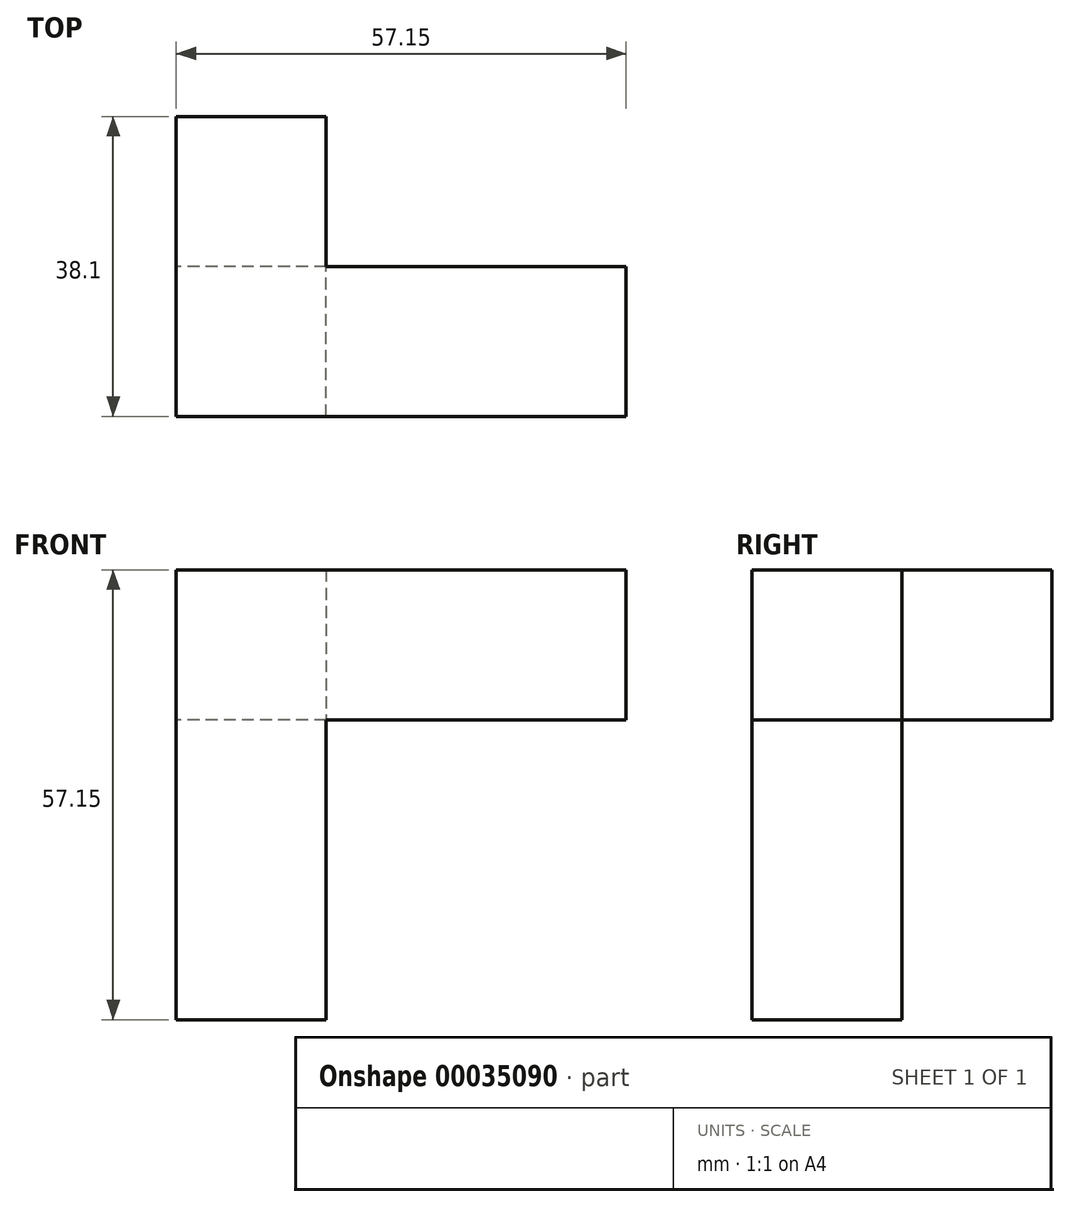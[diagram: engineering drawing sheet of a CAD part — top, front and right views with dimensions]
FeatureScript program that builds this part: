
annotation { "Feature Type Name" : "Feature", "Feature Type Description" : "" }
export const myFeature = defineFeature(function(context is Context, id is Id, definition is map)
    precondition{}
    {
        {
            var Q0;
            Q0=qCreatedBy(makeId("Front.planeOp"),FACE);
            var sketch = newSketch(context, id + "F0", { "sketchPlane" : qUnion([Q0])});
            skLineSegment(sketch, "E0", {"start": v(-68.52, -6.83) * mm, "end": v(-11.37, -6.83) * mm});
            skLineSegment(sketch, "E1", {"start": v(-11.37, -6.83) * mm, "end": v(-11.37, -25.88) * mm});
            skLineSegment(sketch, "E2", {"start": v(-68.52, -6.83) * mm, "end": v(-68.52, -25.88) * mm});
            skLineSegment(sketch, "E3", {"start": v(-68.52, -25.88) * mm, "end": v(-11.37, -25.88) * mm});
            skLineSegment(sketch, "E4", {"start": v(-68.52, -25.88) * mm, "end": v(-68.52, -63.98) * mm});
            skLineSegment(sketch, "E5", {"start": v(-68.52, -63.98) * mm, "end": v(-49.47, -63.98) * mm});
            skLineSegment(sketch, "E6", {"start": v(-49.47, -63.98) * mm, "end": v(-49.47, -25.88) * mm});
            skSolve(sketch);
        }
        {
            var Q0;
            Q0 = qSketchRegion(id + "F0", true);
            extrude(context, id + "F1", {"entities" : qUnion([Q0]), "depth" : 19.05 * mm});
        }
        {
            var Q0;
            Q0=makeQuery(id+"F1.opExtrude","CAP_FACE",FACE,{"disambiguationData":[OSD([sQuery(id+"F0.wireOp",EDGE,"E0"),sQuery(id+"F0.wireOp",EDGE,"E1"),sQuery(id+"F0.wireOp",EDGE,"E2"),sQuery(id+"F0.wireOp",EDGE,"E3"),sQuery(id+"F0.wireOp",EDGE,"E4"),sQuery(id+"F0.wireOp",EDGE,"E5"),sQuery(id+"F0.wireOp",EDGE,"E6")])],"isStart":true});
            var sketch = newSketch(context, id + "F2", { "sketchPlane" : qUnion([Q0])});
            skLineSegment(sketch, "E7", {"start": v(68.52, -6.83) * mm, "end": v(49.47, -6.83) * mm});
            skLineSegment(sketch, "E8", {"start": v(49.47, -6.83) * mm, "end": v(49.47, -25.88) * mm});
            skLineSegment(sketch, "E9", {"start": v(49.47, -25.88) * mm, "end": v(68.52, -25.88) * mm});
            skLineSegment(sketch, "E10", {"start": v(68.52, -6.83) * mm, "end": v(68.52, -25.88) * mm});
            skSolve(sketch);
        }
        {
            var Q0;
            Q0=makeQuery(id+"F2.imprint","IMPRINT",FACE,{"disambiguationData":[TD([[makeQuery(id+"F2.imprint","IMPRINT",EDGE,{"derivedFrom":sQuery(id+"F2.wireOp",EDGE,"E7")}),1.0]])]});
            extrude(context, id + "F3", {"entities" : qUnion([Q0]), "operationType" : NewBodyOperationType.ADD, "depth" : 19.05 * mm});
        }
    });
